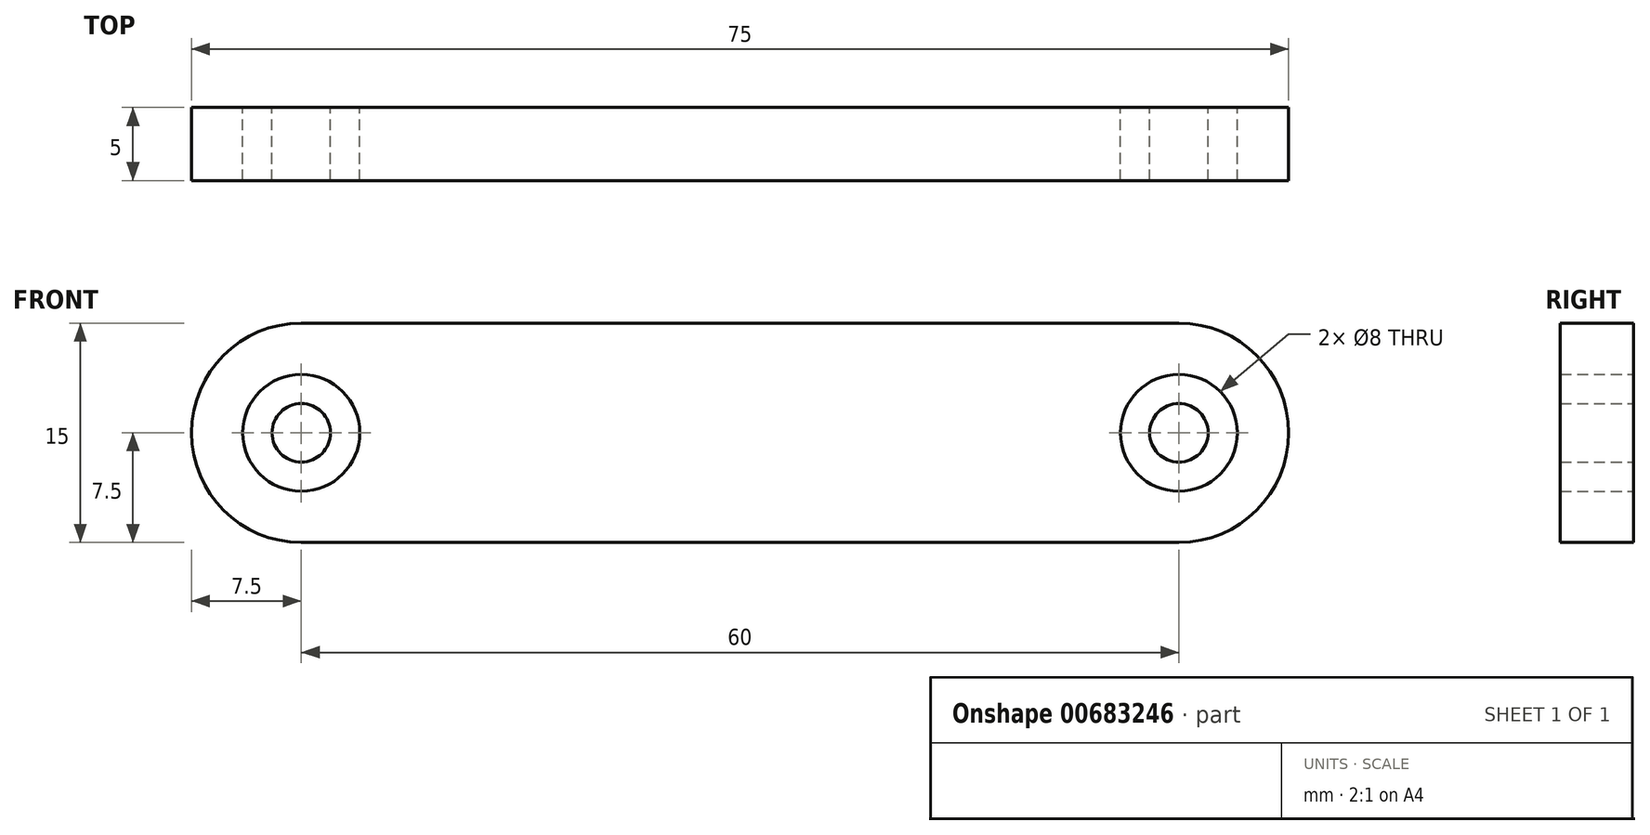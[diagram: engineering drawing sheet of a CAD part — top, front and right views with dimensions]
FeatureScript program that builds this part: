
annotation { "Feature Type Name" : "Feature", "Feature Type Description" : "" }
export const myFeature = defineFeature(function(context is Context, id is Id, definition is map)
    precondition{}
    {
        {
            var Q0;
            Q0=qCreatedBy(makeId("Front.planeOp"),FACE);
            var sketch = newSketch(context, id + "F0", { "sketchPlane" : qUnion([Q0])});
            skLineSegment(sketch, "E0.bottom", {"start": v(0, 0) * mm, "end": v(60, 0) * mm});
            skLineSegment(sketch, "E0.top", {"start": v(0, 15) * mm, "end": v(60, 15) * mm});
            skArc(sketch, "E1", {"start": v(60, 0) * mm, "mid": v(67.5, 7.5) * mm, "end": v(60, 15) * mm});
            skArc(sketch, "E2", {"start": v(0, 15) * mm, "mid": v(-7.5, 7.5) * mm, "end": v(0, 0) * mm});
            skCircle(sketch, "E3", {"center": v(0, 7.5) * mm, "radius": 4 * mm});
            skCircle(sketch, "E4", {"center": v(60, 7.5) * mm, "radius": 4 * mm});
            skCircle(sketch, "E5", {"center": v(60, 7.5) * mm, "radius": 2 * mm});
            skCircle(sketch, "E6", {"center": v(0, 7.5) * mm, "radius": 2 * mm});
            skSolve(sketch);
        }
        {
            var Q0;
            Q0 = qSketchRegion(id + "F0", true);
            var Q1;
            Q1=makeQuery(id+"F0.imprint","IMPRINT",FACE,{"disambiguationData":[TD([[makeQuery(id+"F0.imprint","IMPRINT",EDGE,{"derivedFrom":sQuery(id+"F0.wireOp",EDGE,"E6")}),1.0]])]});
            var Q2;
            Q2=makeQuery(id+"F0.imprint","IMPRINT",FACE,{"disambiguationData":[TD([[makeQuery(id+"F0.imprint","IMPRINT",EDGE,{"derivedFrom":sQuery(id+"F0.wireOp",EDGE,"E5")}),1.0]])]});
            extrude(context, id + "F1", {"entities" : qUnion([Q0, Q1, Q2]), "depth" : 5 * mm, "offsetDistance" : 25 * mm});
        }
    });
